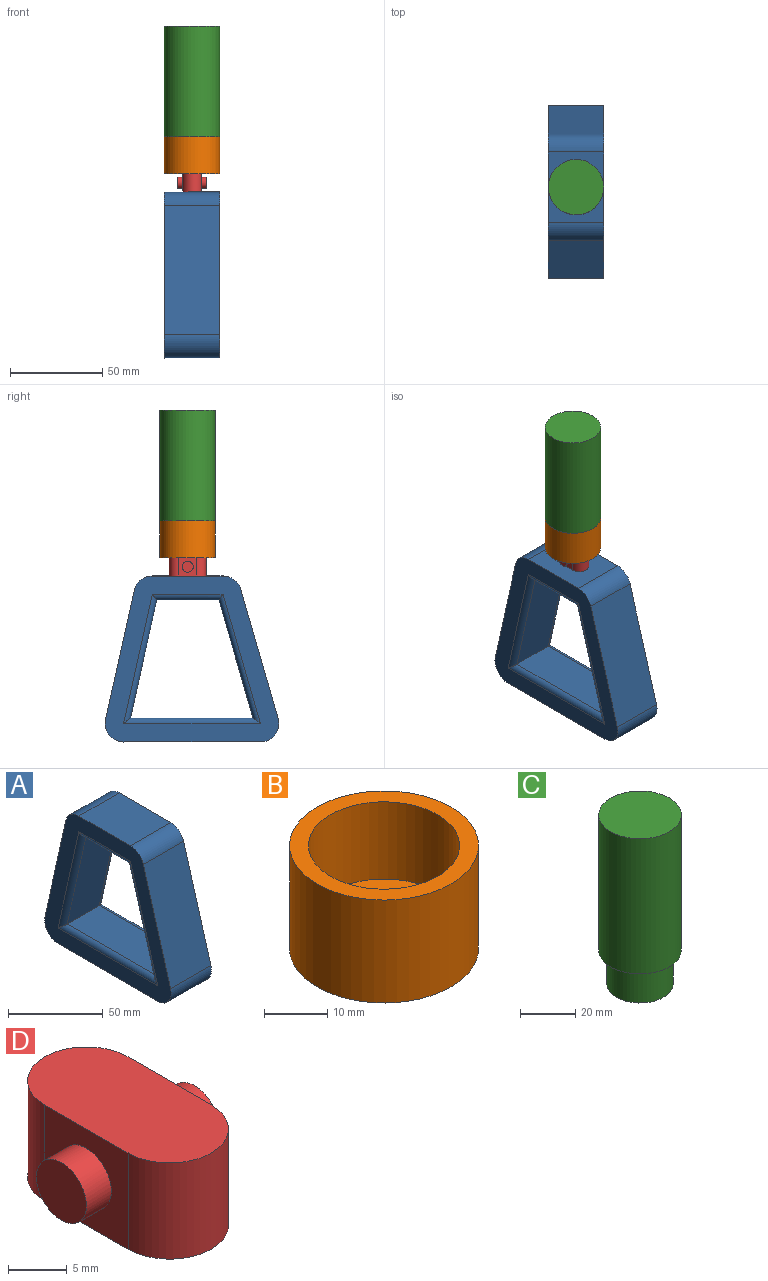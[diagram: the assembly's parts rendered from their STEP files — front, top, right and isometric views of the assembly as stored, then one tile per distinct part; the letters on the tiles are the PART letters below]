
ASSEMBLY  parts=4 mates=3
PART A: 22 faces, bbox 30x94.2x90 mm
  f0: plane 94.22x90mm, normal (1,0,0), area 2886mm2, adj f1,f2,f3,f4,f5,f6,f7,f8
  f1: cylinder r=10mm len=30mm, axis (1,0,0), area 386.6mm2, adj f0,f2,f8,f9
  f2: plane 70x30mm, normal (0,-0.96,0.28), area 2186.5mm2, adj f0,f1,f3,f9
  f3: cylinder r=10mm len=30mm, axis (1,0,0), area 555.9mm2, adj f0,f2,f4,f9
  f4: plane 74.22x30mm, normal (0,0,-1), area 2226.7mm2, adj f0,f3,f5,f9
  f5: cylinder r=10mm len=30mm, axis (1,0,0), area 536.8mm2, adj f0,f4,f6,f9
  f6: plane 70x30mm, normal (0,0.98,0.22), area 2151.2mm2, adj f0,f5,f7,f9
  f7: cylinder r=10mm len=30mm, axis (1,0,0), area 405.6mm2, adj f0,f6,f8,f9
  f8: plane 38.37x30mm, normal (0,0,1), area 1151.2mm2, adj f0,f1,f7,f9
  f9: plane 94.22x90mm, normal (-1,0,0), area 2886mm2, adj f1,f2,f3,f4,f5,f6,f7,f8
  f10: plane 64x24mm, normal (0,0.96,-0.28), area 1599.2mm2, adj f11,f13,f15,f19
  f11: plane 66.49x24mm, normal (0,0,1), area 1595.8mm2, adj f10,f12,f17,f18
  f12: plane 64x24mm, normal (0,-0.98,-0.22), area 1573.5mm2, adj f11,f13,f16,f20
  f13: plane 33.71x24mm, normal (0,0,-1), area 809.1mm2, adj f10,f12,f14,f21
  f14: cylinder r=3mm len=38.37mm, axis (0,-1,0), area 166.9mm2, adj f9,f13,f15,f16
  f15: cylinder r=3mm len=70.84mm, axis (0,-0.28,-0.96), area 324.7mm2, adj f9,f10,f14,f17
  f16: cylinder r=3mm len=70.65mm, axis (0,-0.22,0.98), area 319.5mm2, adj f9,f12,f14,f17
  f17: cylinder r=3mm len=74.22mm, axis (0,1,0), area 326.6mm2, adj f9,f11,f15,f16
  f18: cylinder r=3mm len=74.22mm, axis (0,-1,0), area 326.6mm2, adj f0,f11,f19,f20
  f19: cylinder r=3mm len=70.84mm, axis (0,0.28,0.96), area 324.7mm2, adj f0,f10,f18,f21
  f20: cylinder r=3mm len=70.65mm, axis (0,0.22,-0.98), area 319.5mm2, adj f0,f12,f18,f21
  f21: cylinder r=3mm len=38.37mm, axis (0,1,0), area 166.9mm2, adj f0,f13,f19,f20
PART B: 5 faces, bbox 30x30x20 mm
  f0: cylinder r=12mm len=24mm, axis (0,0,-1), area 1131mm2, adj f2,f4
  f1: cylinder r=15mm len=30mm, axis (0,0,-1), area 1885mm2, adj f2,f3
  f2: plane 30x30mm, normal (0,0,1), area 254.5mm2, adj f0,f1
  f3: plane 30x30mm, normal (0,0,-1), area 706.9mm2, adj f1
  f4: plane 24x24mm, normal (0,0,1), area 452.4mm2, adj f0
PART C: 7 faces, bbox 30x30x75 mm
  f0: cylinder r=15mm len=60mm, axis (0,0,1), area 5654.9mm2, adj f1,f2
  f1: plane 30x30mm, normal (0,0,-1), area 254.5mm2, adj f0,f3
  f2: plane 30x30mm, normal (0,0,1), area 706.9mm2, adj f0
  f3: cylinder r=12mm len=24mm, axis (0,0,1), area 1131mm2, adj f1,f4
  f4: plane 24x24mm, normal (0,0,-1), area 138.2mm2, adj f3,f6
  f5: plane 20x20mm, normal (0,0,-1), area 314.2mm2, adj f6
  f6: cylinder r=10mm len=70mm, axis (0,0,1), area 4398.2mm2, adj f4,f5
PART D: 10 faces, bbox 16x20x10 mm
  f0: plane 10x10mm, normal (-1,0,0), area 71.7mm2, adj f2,f3,f4,f5,f8
  f1: plane 10x10mm, normal (1,0,0), area 71.7mm2, adj f2,f3,f4,f5,f6
  f2: plane 20x10mm, normal (0,0,1), area 178.5mm2, adj f0,f1,f4,f5
  f3: plane 20x10mm, normal (0,0,-1), area 178.5mm2, adj f0,f1,f4,f5
  f4: cylinder r=5mm len=10mm, axis (0,0,-1), area 157.1mm2, adj f0,f1,f2,f3
  f5: cylinder r=5mm len=10mm, axis (0,0,1), area 157.1mm2, adj f0,f1,f2,f3
  f6: cylinder r=3mm len=6mm, axis (-1,0,0), area 56.5mm2, adj f1,f7
  f7: plane 6x6mm, normal (1,0,0), area 28.3mm2, adj f6
  f8: cylinder r=3mm len=6mm, axis (1,0,0), area 56.5mm2, adj f0,f9
  f9: plane 6x6mm, normal (-1,0,0), area 28.3mm2, adj f8
PLACE A rot(axis=(-0.05,-0.88,-0.48),0deg) t=(-186.21,-151.59,52.86)mm
PLACE B rot(axis=(-0.05,-0.88,-0.48),0deg) t=(-186.21,-148.8,102.86)mm
PLACE C rot(axis=(-0.05,-0.88,-0.48),0deg) t=(-186.21,-148.8,182.86)mm fixed
PLACE D rot(axis=(-0.05,-0.88,-0.48),0deg) t=(-186.21,-148.8,92.86)mm
MATE fastened D.f2 <-> B.f1  axis (0,0,1) through (-186.21,-148.8,102.86)mm
MATE fastened D.f3 <-> A.f8  axis (0,0,-1) through (-186.21,-148.8,92.86)mm
MATE cylindrical C.f6 <-> B.f0  axis (0,0,1) through (-186.21,-148.8,107.86)mm
